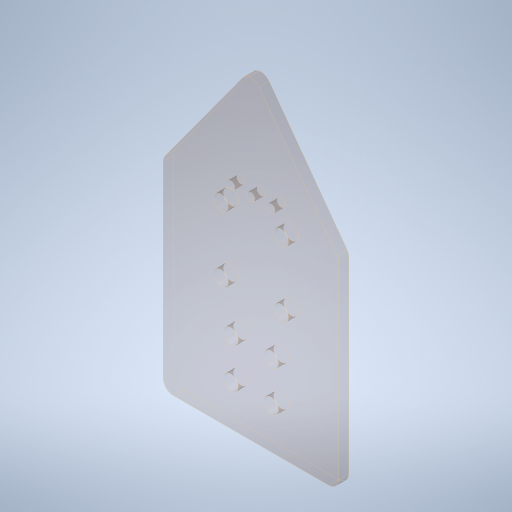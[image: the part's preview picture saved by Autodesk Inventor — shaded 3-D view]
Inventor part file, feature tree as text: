
AUTODESK INVENTOR PART (.ipt)
format: ipt  version: 2023.4 (Build 274418000, 418)  size: 319,488 bytes
history: native  units: in
note: dims shown in document units (in); Inventor stores cm internally (conversion verified against a paired STEP export)
features: sketch x4, hole x2, projected_geometry x2, extrude x1, fillet x1, mirror x1
ambient origin geometry x8: Origin, YZ Plane, XZ Plane, XY Plane, X Axis, Y Axis, Z Axis, Center Point
bodies: Solid1 (feature_tree)
feature tree (11):
  extrude  "Extrusion1"  Depth=3.0in
  hole  "Hole1"  [1 undecoded]
  fillet  "Fillet2"  Radius=5.0in
  sketch  "Sketch3"  dims[d7=0.201in d8=0.38in d9=0.385in d10=0.25in d11=0.5635in d12=1.0in d13=0.8108in d14=5.0in]
  hole  "Hole2"  [1 undecoded]
  mirror  "Mirror1"
  sketch  "Sketch1"  dims[d0=4.375in d1=3.0in]
  sketch  "Sketch2"  dims[d2=0.25in d3=0.0in d6=1.0in]
  projected_geometry  "Projected Loop1"
  sketch  "Sketch4"  dims[d15=5.25in d16=0.25in d17=1.0in d24=0.5in d25=0.75in d26=2.125in d27=0.75in d28=0.5in d29=3.25in d30=4.25in d33=0.375in d34=0.75in d35=0.563in d36=0.12in d37=0.5635in d38=1.0in d39=0.8108in]
  projected_geometry  "Projected Loop2"
note: 2 required parameter values undecoded (feature->parameter linkage not recoverable at this tier; creation-order binding heuristic only, values carry confidence <= 0.55)
